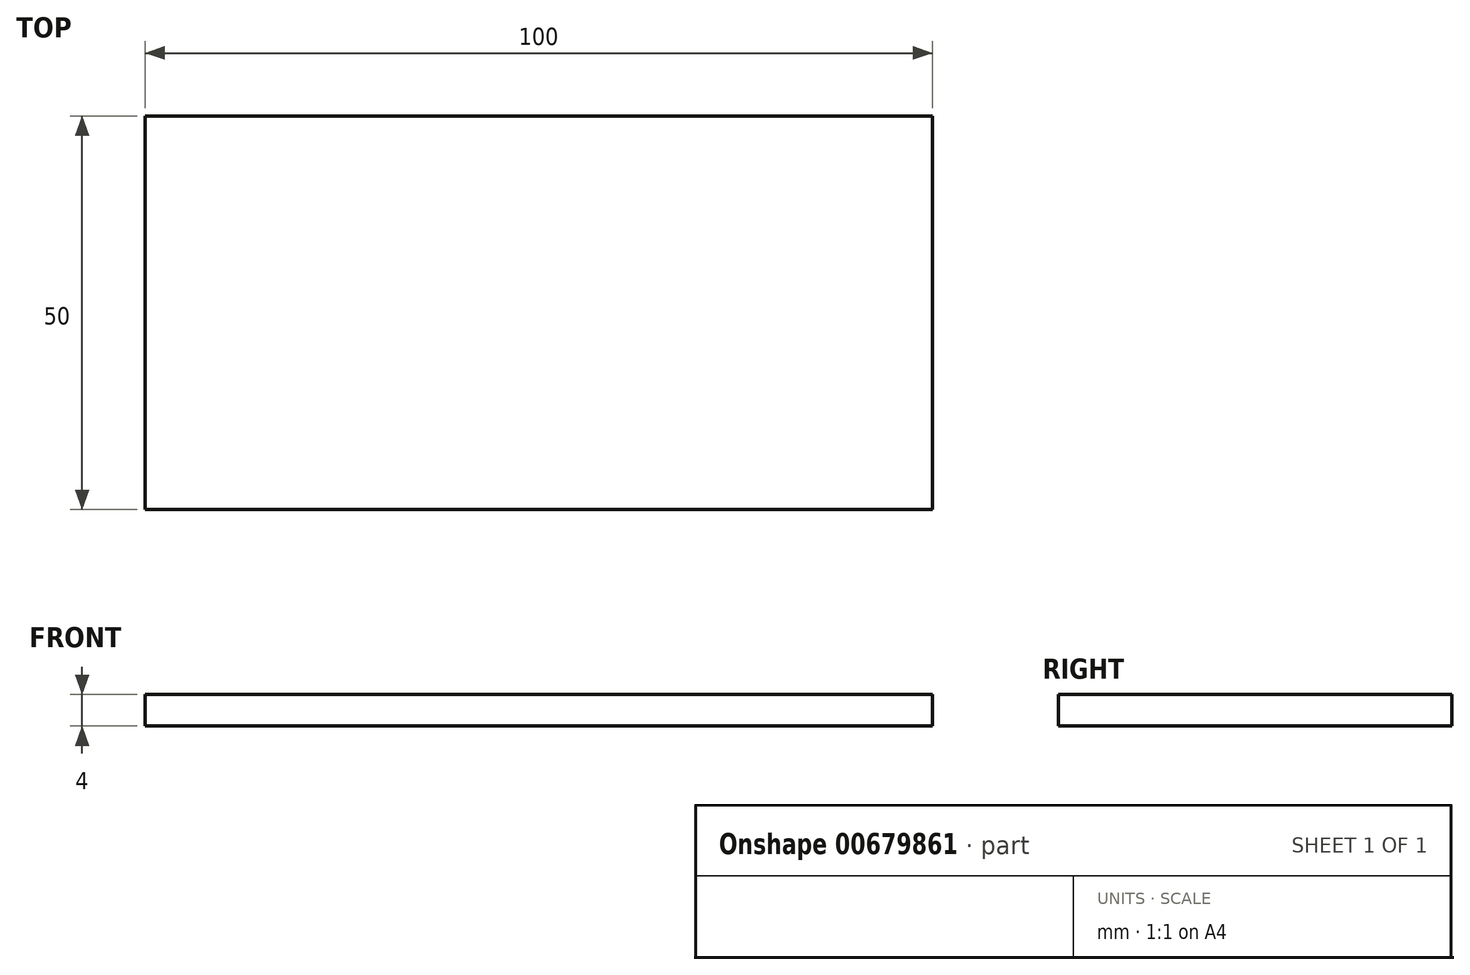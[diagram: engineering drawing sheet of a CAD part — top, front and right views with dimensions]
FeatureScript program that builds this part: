
annotation { "Feature Type Name" : "Feature", "Feature Type Description" : "" }
export const myFeature = defineFeature(function(context is Context, id is Id, definition is map)
    precondition{}
    {
        {
            var Q0;
            Q0=qCreatedBy(makeId("Top.planeOp"),FACE);
            var sketch = newSketch(context, id + "F0", { "sketchPlane" : qUnion([Q0])});
            skLineSegment(sketch, "E0.bottom", {"start": v(-49.82, 50.13) * mm, "end": v(50.18, 50.13) * mm});
            skLineSegment(sketch, "E0.top", {"start": v(-49.82, 0.13) * mm, "end": v(50.18, 0.13) * mm});
            skLineSegment(sketch, "E0.left", {"start": v(-49.82, 50.13) * mm, "end": v(-49.82, 0.13) * mm});
            skLineSegment(sketch, "E0.right", {"start": v(50.18, 50.13) * mm, "end": v(50.18, 0.13) * mm});
            skSolve(sketch);
        }
        {
            var Q0;
            Q0=makeQuery(id+"F0.imprint","IMPRINT",FACE,{"disambiguationData":[TD([[makeQuery(id+"F0.imprint","IMPRINT",EDGE,{"derivedFrom":sQuery(id+"F0.wireOp",EDGE,"E0.bottom")}),-1.0]])]});
            extrude(context, id + "F1", {"entities" : qUnion([Q0]), "depth" : 4 * mm, "offsetDistance" : 25 * mm});
        }
    });
